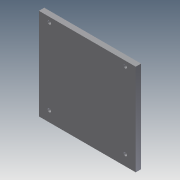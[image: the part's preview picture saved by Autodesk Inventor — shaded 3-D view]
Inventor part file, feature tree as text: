
AUTODESK INVENTOR PART (.ipt)
format: ipt  version: 2011 (Build 150239000, 239)  size: 179,712 bytes
history: native  units: in
note: dims shown in document units (in); Inventor stores cm internally (conversion verified against a paired STEP export)
features: extrude x13, sketch x13, fillet x1
ambient origin geometry x8: Origin, YZ Plane, XZ Plane, XY Plane, X Axis, Y Axis, Z Axis, Center Point
bodies: Solid1 (feature_tree)
feature tree (27):
  extrude  "Extrusion1"  Depth=4.0in
  extrude  "Extrusion2"  Depth=2.16in
  extrude  "Extrusion3"  Depth=1.7655in
  extrude  "Extrusion4"  Depth=0.029in TaperAngle=0.0deg
  extrude  "Extrusion5"  Depth=2.36in
  fillet  "Fillet1"  Radius=2.56in
  extrude  "Extrusion6"  Depth=0.125in
  extrude  "Extrusion7"  Depth=0.25in TaperAngle=0.0deg
  extrude  "Extrusion8"  Depth=0.25in
  extrude  "Extrusion9"  Depth=1.0in TaperAngle=0.0deg
  extrude  "Extrusion10"  Depth=0.25in TaperAngle=0.0deg
  extrude  "Extrusion11"  Depth=0.25in TaperAngle=0.0deg
  extrude  "Extrusion12"  [1 undecoded]
  extrude  "Extrusion13"  [1 undecoded]
  sketch  "Sketch1"  dims[d0=4.0in d1=4.0in]
  sketch  "Sketch2"  dims[d2=0.029in d3=0.0in d4=2.16in]
  sketch  "Sketch3"  dims[d5=0.029in d6=0.0in d7=1.7655in]
  sketch  "Sketch4"  dims[d8=0.156in d9=0.029in d10=0.0in]
  sketch  "Sketch5"  dims[d11=0.029in d12=0.0in d13=2.36in d14=2.56in]
  sketch  "Sketch6"  dims[d15=0.262in d16=0.0in d17=0.125in]
  sketch  "Sketch7"  dims[d18=0.25in d19=0.0in d20=0.25in d21=0.0in]
  sketch  "Sketch8"  dims[d22=0.25in d23=0.25in]
  sketch  "Sketch9"  dims[d24=0.5in d25=1.0in d26=0.0in]
  sketch  "Sketch10"  dims[d27=1.0in d28=0.0in d29=0.25in d30=0.0in]
  sketch  "Sketch11"  dims[d31=0.25in d32=0.0in d33=0.25in d34=0.0in]
  sketch  "Sketch12"  dims[d35=0.25in d36=0.0in]
  sketch  "Sketch13"
note: 2 required parameter values undecoded (feature->parameter linkage not recoverable at this tier; creation-order binding heuristic only, values carry confidence <= 0.55)
